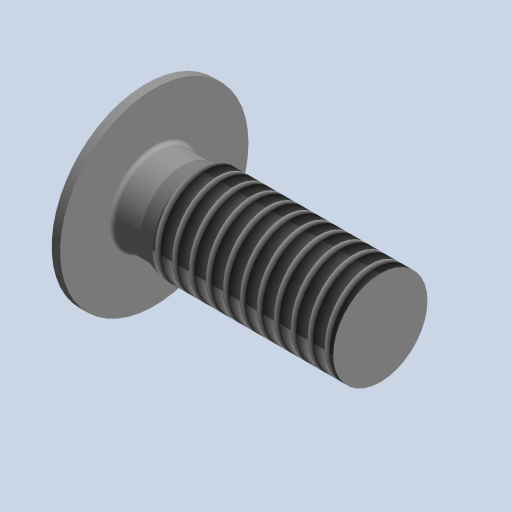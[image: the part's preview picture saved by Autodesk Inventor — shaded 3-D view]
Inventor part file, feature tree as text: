
AUTODESK INVENTOR PART (.ipt)
format: ipt  version: 2023 (Build 270158000, 158)  size: 152,064 bytes
history: native  units: mm (DEFAULTED — no unit token found)
features: other x1, fillet x1, thread x1
ambient origin geometry x8: Origin, YZ Plane, XZ Plane, XY Plane, X Axis, Y Axis, Z Axis, Center Point
bodies: Body1 (feature_tree)
feature tree (3):
  other  "ソリッド1"
  fillet  "Fillet1"  Radius=7.06263mm
  thread  "ねじ1"
